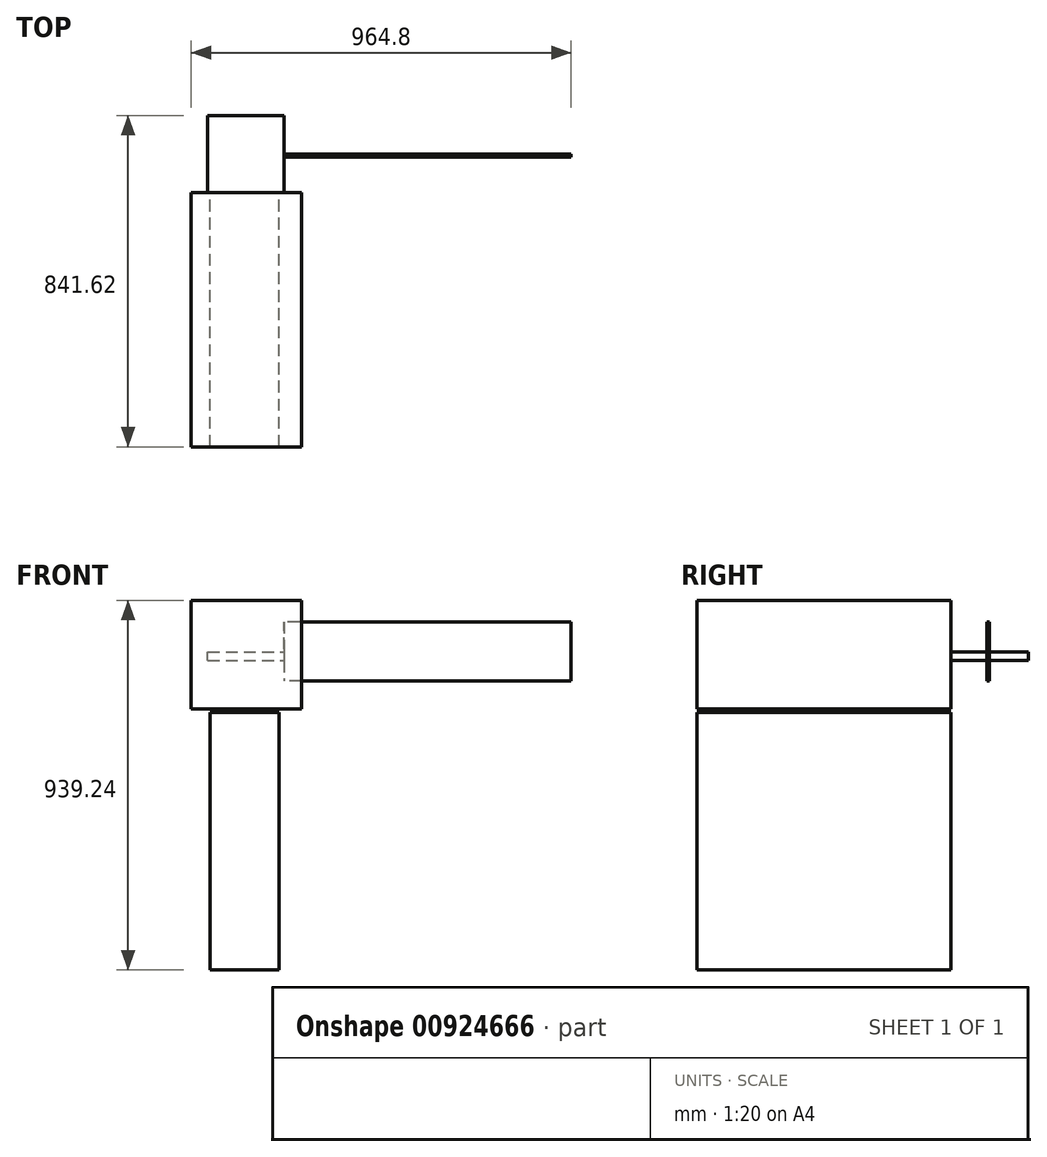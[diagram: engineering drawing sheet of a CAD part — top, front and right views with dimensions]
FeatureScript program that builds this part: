
annotation { "Feature Type Name" : "Feature", "Feature Type Description" : "" }
export const myFeature = defineFeature(function(context is Context, id is Id, definition is map)
    precondition{}
    {
        {
            var Q0;
            Q0=qCreatedBy(makeId("Top.planeOp"),FACE);
            var sketch = newSketch(context, id + "F0", { "sketchPlane" : qUnion([Q0])});
            skLineSegment(sketch, "E0.bottom", {"start": v(-96.58, -97.84) * mm, "end": v(97.5, -97.84) * mm});
            skLineSegment(sketch, "E0.top", {"start": v(-96.58, 98.3) * mm, "end": v(97.5, 98.3) * mm});
            skLineSegment(sketch, "E0.left", {"start": v(-96.58, -97.84) * mm, "end": v(-96.58, 98.3) * mm});
            skLineSegment(sketch, "E0.right", {"start": v(97.5, -97.84) * mm, "end": v(97.5, 98.3) * mm});
            skSolve(sketch);
        }
        {
            var Q0;
            Q0 = qSketchRegion(id + "F0", true);
            extrude(context, id + "F1", {"entities" : qUnion([Q0]), "oppositeDirection" : true, "depth" : 21.64 * mm, "offsetDistance" : 25.4 * mm});
        }
        {
            var Q0;
            Q0=makeQuery(id+"F1.opExtrude","SWEPT_FACE",FACE,{"disambiguationData":[OSD([sQuery(id+"F0.wireOp",EDGE,"E0.right")])]});
            var sketch = newSketch(context, id + "F2", { "sketchPlane" : qUnion([Q0])});
            skLineSegment(sketch, "E1", {"start": v(0, 7.1) * mm, "end": v(0, 76.83) * mm});
            skLineSegment(sketch, "E2", {"start": v(0, 76.83) * mm, "end": v(-7.1, 76.83) * mm});
            skLineSegment(sketch, "E3", {"start": v(-7.1, 76.83) * mm, "end": v(-7.1, 0) * mm});
            skLineSegment(sketch, "E4", {"start": v(-7.1, 0) * mm, "end": v(-7.1, -73.8) * mm});
            skLineSegment(sketch, "E5", {"start": v(-7.1, -73.8) * mm, "end": v(0, 7.1) * mm});
            skLineSegment(sketch, "E6", {"start": v(0, 7.1) * mm, "end": v(-7.1, -73.8) * mm});
            skLineSegment(sketch, "E7", {"start": v(0, 7.1) * mm, "end": v(0.23, -74.05) * mm});
            skPoint(sketch, "E7.endSnap0", {"position": v(0.23, -21.64) * mm});
            skLineSegment(sketch, "E8", {"start": v(0.23, -74.05) * mm, "end": v(-7.1, -73.8) * mm});
            skSolve(sketch);
        }
        {
            var Q0;
            Q0 = qSketchRegion(id + "F2", true);
            extrude(context, id + "F3", {"entities" : qUnion([Q0]), "operationType" : NewBodyOperationType.ADD, "depth" : 728.67 * mm, "offsetDistance" : 25.4 * mm});
        }
        {
            var Q0;
            Q0=makeQuery(id+"F1.opExtrude","SWEPT_FACE",FACE,{"disambiguationData":[OSD([sQuery(id+"F0.wireOp",EDGE,"E0.bottom")])]});
            var sketch = newSketch(context, id + "F4", { "sketchPlane" : qUnion([Q0])});
            skLineSegment(sketch, "E9.bottom", {"start": v(-90.92, -153.7) * mm, "end": v(84.86, -153.7) * mm});
            skLineSegment(sketch, "E9.top", {"start": v(-90.92, -807.93) * mm, "end": v(84.86, -807.93) * mm});
            skLineSegment(sketch, "E9.left", {"start": v(-90.92, -153.7) * mm, "end": v(-90.92, -807.93) * mm});
            skLineSegment(sketch, "E9.right", {"start": v(84.86, -153.7) * mm, "end": v(84.86, -807.93) * mm});
            skLineSegment(sketch, "E10.bottom", {"start": v(141.14, -145.18) * mm, "end": v(-138.63, -145.18) * mm});
            skLineSegment(sketch, "E10.top", {"start": v(141.14, 131.31) * mm, "end": v(-138.63, 131.31) * mm});
            skLineSegment(sketch, "E10.left", {"start": v(141.14, -145.18) * mm, "end": v(141.14, 131.31) * mm});
            skLineSegment(sketch, "E10.right", {"start": v(-138.63, -145.18) * mm, "end": v(-138.63, 131.31) * mm});
            skSolve(sketch);
        }
        {
            var Q0;
            Q0 = qSketchRegion(id + "F4", true);
            extrude(context, id + "F5", {"entities" : qUnion([Q0]), "operationType" : NewBodyOperationType.ADD, "depth" : 645.5 * mm, "offsetDistance" : 25.4 * mm});
        }
    });
